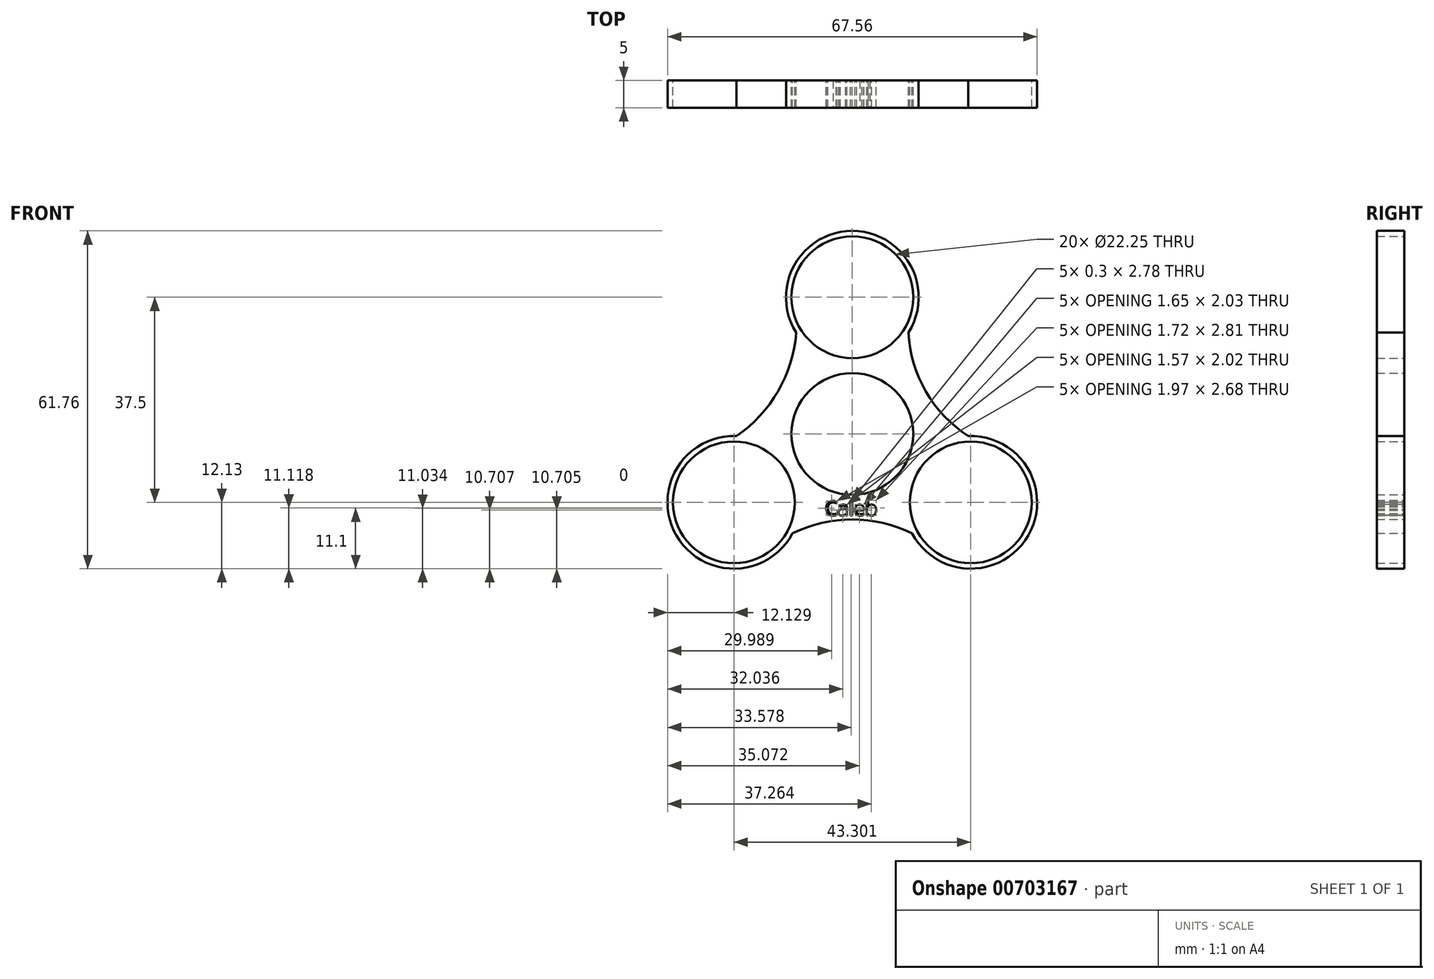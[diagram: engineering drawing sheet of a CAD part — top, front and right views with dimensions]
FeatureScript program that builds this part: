
annotation { "Feature Type Name" : "Feature", "Feature Type Description" : "" }
export const myFeature = defineFeature(function(context is Context, id is Id, definition is map)
    precondition{}
    {
        {
            var Q0;
            Q0=qCreatedBy(makeId("Front.planeOp"),FACE);
            var sketch = newSketch(context, id + "F0", { "sketchPlane" : qUnion([Q0])});
            skCircle(sketch, "E0", {"center": v(0, 0) * mm, "radius": 11.12 * mm});
            skCircle(sketch, "E1", {"center": v(0, 25) * mm, "radius": 11.12 * mm});
            skCircle(sketch, "E2", {"center": v(21.65, -12.5) * mm, "radius": 11.12 * mm});
            skCircle(sketch, "E3", {"center": v(-21.65, -12.5) * mm, "radius": 11.12 * mm});
            skArc(sketch, "E4", {"start": v(10.26, 18.53) * mm, "mid": v(0, 37.13) * mm, "end": v(-10.26, 18.53) * mm});
            skArc(sketch, "E5.1.0", {"start": v(-21.18, -0.38) * mm, "mid": v(-32.15, -18.56) * mm, "end": v(-10.92, -18.15) * mm});
            skArc(sketch, "E5.2.0", {"start": v(10.92, -18.15) * mm, "mid": v(32.15, -18.56) * mm, "end": v(21.18, -0.38) * mm});
            skArc(sketch, "E6", {"start": v(12.12, 25.49) * mm, "mid": v(12.11, 24.99) * mm, "end": v(12.11, 24.49) * mm});
            skArc(sketch, "E7", {"start": v(21.13, -1.39) * mm, "mid": v(21.16, -0.89) * mm, "end": v(21.18, -0.38) * mm});
            skArc(sketch, "E8.trimOffspring", {"start": v(-9.37, 19) * mm, "mid": v(-9.81, 18.77) * mm, "end": v(-10.26, 18.53) * mm});
            skArc(sketch, "E9.trimOffspring", {"start": v(-11.77, -17.6) * mm, "mid": v(-11.35, -17.88) * mm, "end": v(-10.92, -18.15) * mm});
            skArc(sketch, "E10", {"start": v(-21.18, -0.38) * mm, "mid": v(-13.57, 7.83) * mm, "end": v(-10.26, 18.53) * mm});
            skArc(sketch, "E11", {"start": v(10.26, 18.53) * mm, "mid": v(13.44, 7.76) * mm, "end": v(21.18, -0.38) * mm});
            skArc(sketch, "E12", {"start": v(10.92, -18.15) * mm, "mid": v(0, -15.64) * mm, "end": v(-10.92, -18.15) * mm});
            skArc(sketch, "E13.trimOffspring", {"start": v(-21.18, -0.38) * mm, "mid": v(-21.16, -0.89) * mm, "end": v(-21.13, -1.39) * mm});
            skArc(sketch, "E14.trimOffspring", {"start": v(10.26, 18.53) * mm, "mid": v(9.81, 18.77) * mm, "end": v(9.37, 19) * mm});
            skArc(sketch, "E15.trimOffspring", {"start": v(10.92, -18.15) * mm, "mid": v(11.35, -17.88) * mm, "end": v(11.77, -17.6) * mm});
            skText(sketch, "E16", { "text": "Caleb", "fontName": "OpenSans-Regular.ttf"});
            const initialGuessF0  = {"E16": [-0.005, -0.0149, 1, 0, 0.00263]};
            skSetInitialGuess(sketch, initialGuessF0);
            skSolve(sketch);
        }
        {
            var Q0;
            Q0 = qSketchRegion(id + "F0", true);
            extrude(context, id + "F1", {"entities" : qUnion([Q0]), "depth" : 5 * mm, "offsetDistance" : 25 * mm});
        }
    });
